# Revit family: BC_Hitachi_RPK-FSRHM_LOD400
name_source: partatom
category: Mechanical Equipment
revit_build: Autodesk Revit 2018 (Build: 20170223_1515(x64)
units: mm (PartAtom-declared; Revit-internal decimal feet)

## family parameters
Cut with Voids When Loaded = No
Host = Face
OmniClass Number = 23.75.00.00
OmniClass Title = Climate Control (HVAC)
Part Type = Normal
Room Calculation Point = No
Round Connector Dimension = Use Diameter
Shared = No

## types (10) — shared parameters
BC_OBJECT_ID = 209117
BC_OBJECT_VERSION = #21
Default Elevation = 1219.20 mm
Description = Wall Hung without electronic expansion valve inside
Diameter left side pipe wire hole = 65.00 mm
Diameter right side pipe wire hole = 65.00 mm
Engine Power = 40 W
Frequency = 50 Hz
Gas Diameter = 12.70 mm
Liquid Diameter = 6.35 mm
Manufacturer = Hitachi Air Conditioning Europe SAS
MasterFormat = Indoor Central-Station Air-Handling Units
Masterformat Code = 23 73 00
Maximum Current = 5 A
Model = Indoor unit - Wall hung RPK - FSR(H)M
Name BIM&CO = Indoor Unit
Nominal Voltage = 230 V
OmniClass code = 23-33 25 00
OmniClass description = Air Handling Units
Operation and service space = Yes
Operation and service space - Material = Operation and service space
Operation and service space - a = 150.00 mm
Operation and service space - b = 100.00 mm
Operation and service space - c = 100.00 mm
Operation and service space - d = 1000.00 mm
Outlet Diameter = 20.00 mm
Overall depth = 230.00 mm
Overall height = 300.00 mm
Refrigerant Type = R410A / R32
Refrigerant pipe connection = Flare nuts
Remote control = PC-ARFP1E / PC-AWR (*)
Uniformat = Distribution Systems

## per-type parameters (varying)
| type | Air Flow - Speed Hi | Air Flow - Speed Medium | BC_VARIANT_ID | Cooling Capacity | Distance Gas pipe | Distance rear left side pipe wire hole | Distance rear right side pipe wire hole | Heating Capacity | Net Weight | Nominal cooling capacity (UTOPIA) | Nominal heating capacity (UTOPIA) | Overall width | Packaging volume | Product Code | Reference | Sound Power Min | Sound power level - Speed Hi2 (dB(A)) | Sound power level - Speed Medium (dB(A)) | Sound pressure level - Speed Hi (dB(A)) | Sound pressure level - Speed Hi2 (dB(A)) | Sound pressure level - Speed Low (dB(A)) | Sound pressure level - Speed Medium (dB(A)) |
| RPK-1.5FSRM | 660.0 m³/h | 540.0 m³/h | 508760 | 4 kW | 107.00 mm | 136.00 mm | 107.00 mm | 5 kW | 11.00 kg | 4 kW | 4 kW | 900.00 mm | 0.11 m³ | 60279208 | RPK-1.5FSRM | 47 | 58 | 50 | 40 | 46 | 36 | 33 |
| RPK-1.0FSRM | 480.0 m³/h | 420.0 m³/h | 508762 | 3 kW | 107.00 mm | 45.00 mm | 107.00 mm | 3 kW | 10.00 kg | 3 kW | 3 kW | 790.00 mm | 0.09 m³ | 60279207 | RPK-1.0FSRM | 45 | 43 | 47 | 35 | 39 | 32 | 30 |
| RPK-0.8FSRM | 480.0 m³/h | 420.0 m³/h | 508757 | 2 kW | 107.00 mm | 45.00 mm | 107.00 mm | 3 kW | 10.00 kg | 2 kW | 2 kW | 790.00 mm | 0.09 m³ | 60279206 | RPK-0.8FSRM | 45 | 53 | 47 | 35 | 39 | 32 | 30 |
| RPK-0.4FSRM | 438.0 m³/h | 402.0 m³/h | 508755 | 1 kW | 100.00 mm | 45.00 mm | 100.00 mm | 1 kW | 9.00 kg | 0 kW | 0 kW | 790.00 mm | 0.09 m³ | 60279204 | RPK-0.4FSRM | 45 | 49 | 46 | 31 | 32 | 30 | 29 |
| RPK-0.4FSRHM | 438.0 m³/h | 402.0 m³/h | 508756 | 1 kW | 100.00 mm | 45.00 mm | 100.00 mm | 1 kW | 9.00 kg | 0 kW | 0 kW | 790.00 mm | 0.09 m³ | 60279221 | RPK-0.4FSRHM | 45 | 49 | 46 | 31 | 32 | 30 | 29 |
| RPK-0.6FSRM | 450.0 m³/h | 420.0 m³/h | 508761 | 3 kW | 100.00 mm | 45.00 mm | 100.00 mm | 3 kW | 10.00 kg | 0 kW | 0 kW | 790.00 mm | 0.09 m³ | 60279207 | RPK-1.0FSRM | 45 | 49 | 46 | 32 | 35 | 31 | 29 |
| RPK-0.6FSRHM | 450.0 m³/h | 420.0 m³/h | 508753 | 2 kW | 100.00 mm | 45.00 mm | 100.00 mm | 2 kW | 10.00 kg | 0 kW | 0 kW | 790.00 mm | 0.09 m³ | 60279222 | RPK-0.6FSRHM | 45 | 49 | 46 | 32 | 35 | 31 | 29 |
| RPK-0.8FSRHM | 480.0 m³/h | 420.0 m³/h | 508758 | 2 kW | 107.00 mm | 45.00 mm | 107.00 mm | 3 kW | 10.00 kg | 2 kW | 2 kW | 790.00 mm | 0.09 m³ | 60279223 | RPK-0.8FSRHM | 45 | 53 | 47 | 35 | 39 | 32 | 30 |
| RPK-1.0FSRHM | 480.0 m³/h | 420.0 m³/h | 508754 | 3 kW | 107.00 mm | 45.00 mm | 107.00 mm | 3 kW | 10.00 kg | 3 kW | 3 kW | 790.00 mm | 0.09 m³ | 60279224 | RPK-1.0FSRHM | 45 | 43 | 47 | 35 | 39 | 32 | 30 |
| RPK-1.5FSRHM | 660.0 m³/h | 540.0 m³/h | 508759 | 4 kW | 107.00 mm | 136.00 mm | 107.00 mm | 5 kW | 11.00 kg | 4 kW | 4 kW | 900.00 mm | 0.11 m³ | 60279225 | RPK-1.5FSRHM | 47 | 58 | 50 | 40 | 46 | 36 | 33 |

note: column(s) folded — value = type name in every type: Type Comments
